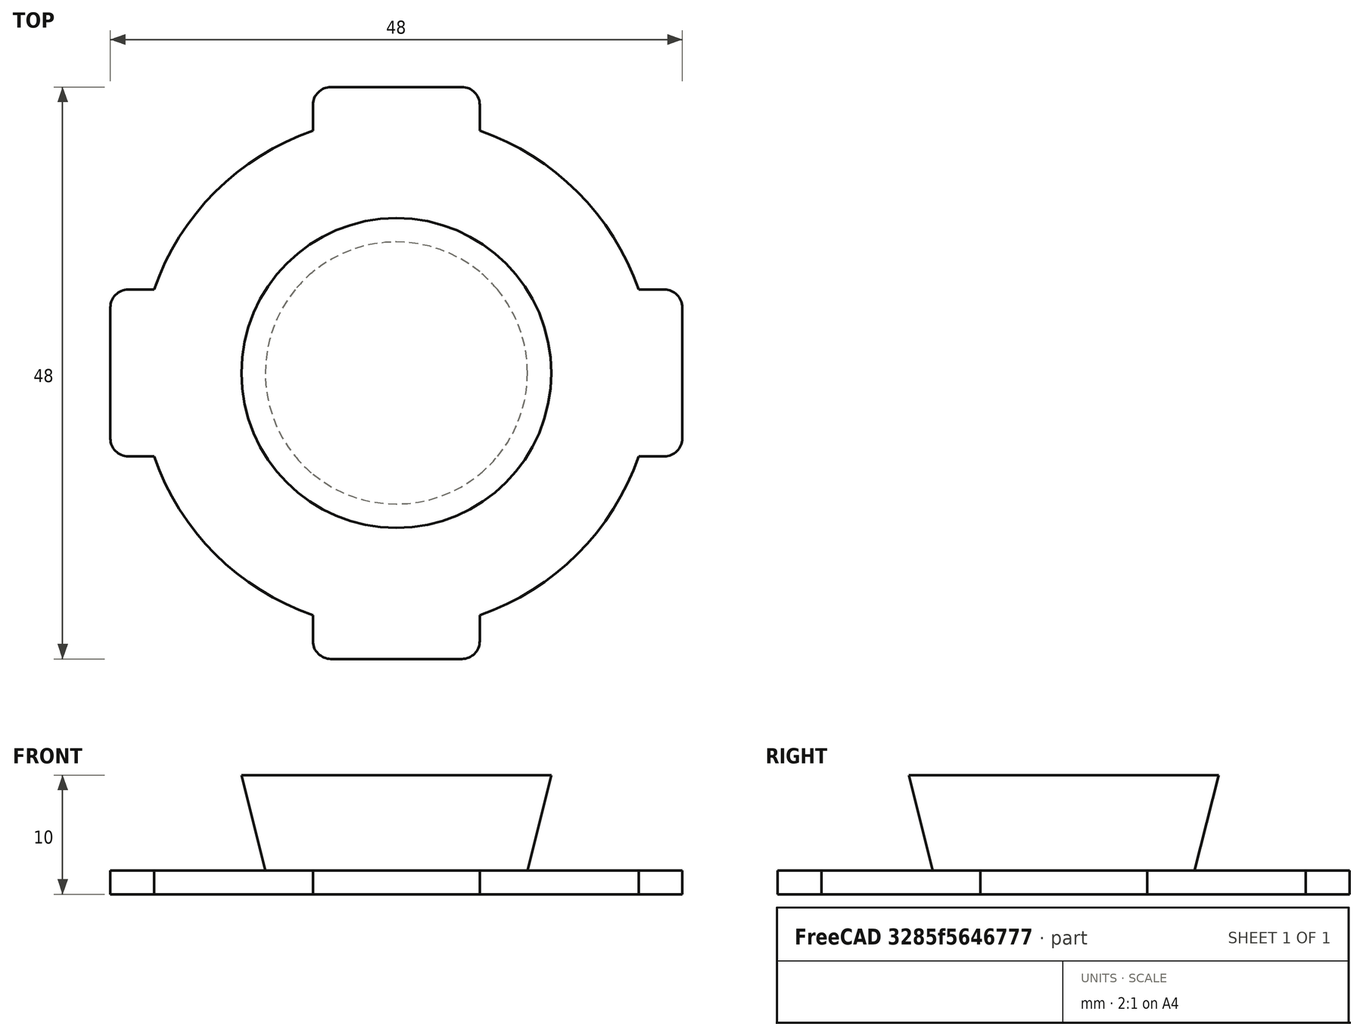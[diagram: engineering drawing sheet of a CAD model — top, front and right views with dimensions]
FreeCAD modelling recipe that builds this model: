
FCSTD DOCUMENT  (FreeCAD 0.17R13541 (Git))
Label: kinor-35-videotap-port-cover
License: All rights reserved
LicenseURL: http://en.wikipedia.org/wiki/All_rights_reserved
objects: Part::Box×2, Part::Fillet×2, Part::Cylinder×1, Part::Cone×1, Part::MultiFuse×1
note: 7 computed .brp shape members not serialized (recipe doc carries the construction recipe); baked Part::Feature solids carry a one-line shape summary decoded from their .brp

FEATURE [Part::Cylinder] Cylinder
  Angle = 360
  AttacherType = Attacher::AttachEngine3D
  Height = 2
  Radius = 21.5
FEATURE [Part::Box] Box  label="Cube"
  AttacherType = Attacher::AttachEngine3D
  Height = 2
  Length = 14
  Placement = pos=(-7,-24,0) rot=(0,0,1;0rad)
  Width = 48
FEATURE [Part::Box] Box001  label="Cube001"
  AttacherType = Attacher::AttachEngine3D
  Height = 2
  Length = 48
  Placement = pos=(-24,-7,0) rot=(0,0,1;0rad)
  Width = 14
FEATURE [Part::Fillet] Fillet
  Base = -> Box
  Edges = 4 edges r=1.5: [Edge1,Edge3,Edge5,Edge7]
FEATURE [Part::Fillet] Fillet001
  Base = -> Box001
  Edges = 4 edges r=1.5: [Edge1,Edge3,Edge5,Edge7]
FEATURE [Part::Cone] Cone
  Angle = 360
  AttacherType = Attacher::AttachEngine3D
  Height = 8
  Placement = pos=(0,0,2) rot=(0,0,1;0rad)
  Radius1 = 11
  Radius2 = 13
FEATURE [Part::MultiFuse] Fusion  label="Videotap Port Cover"
  Shapes = -> [Cylinder,Cone,Fillet,Fillet001]
